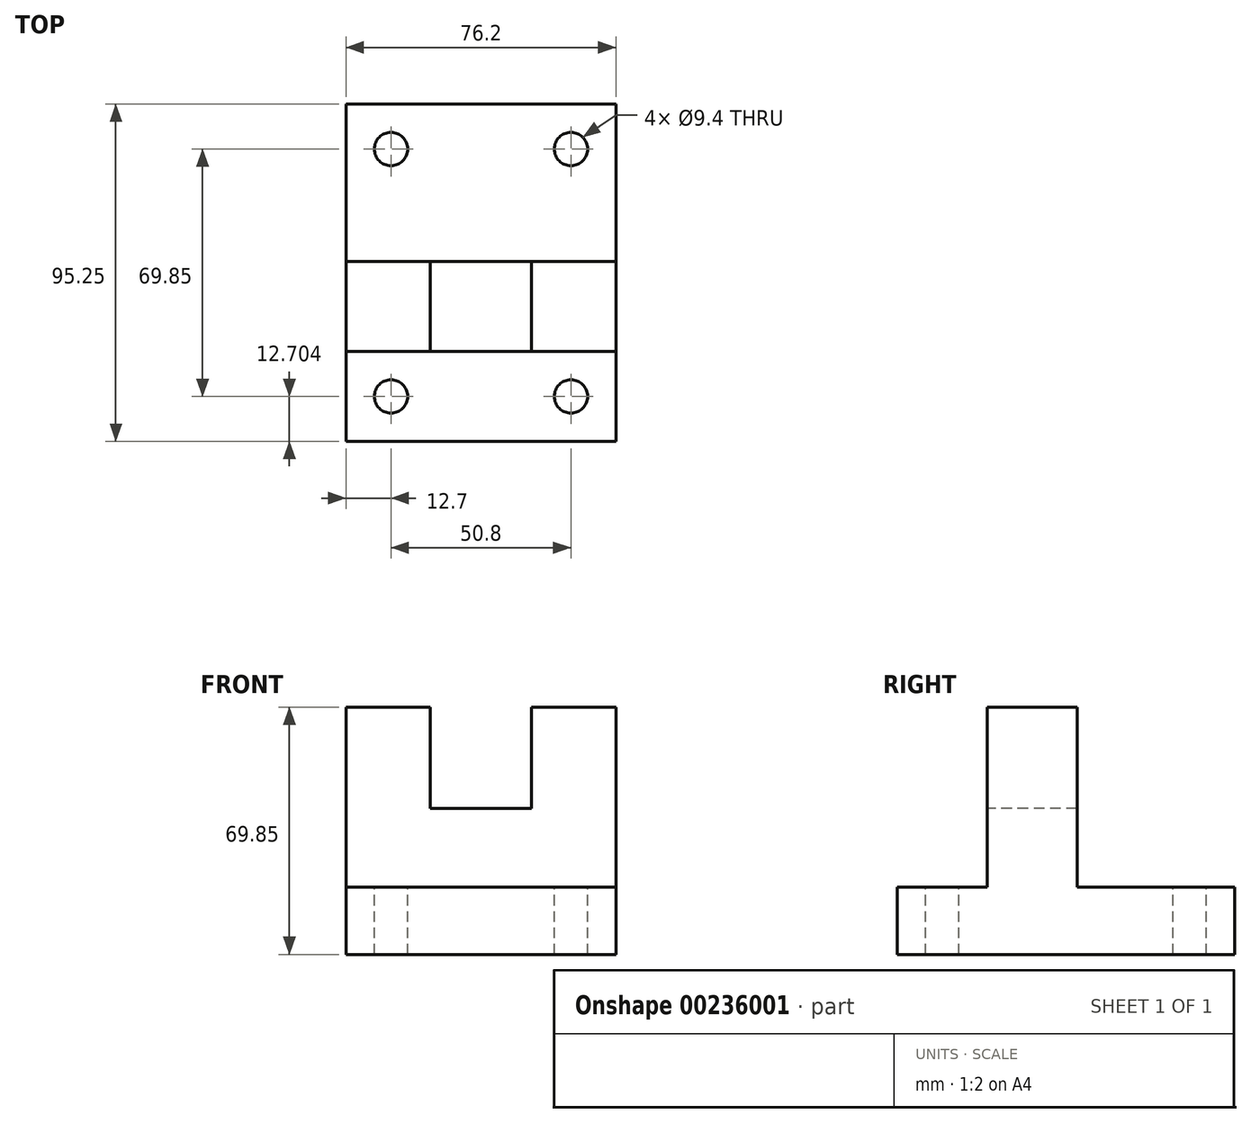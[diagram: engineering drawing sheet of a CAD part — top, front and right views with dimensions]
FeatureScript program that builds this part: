
annotation { "Feature Type Name" : "Feature", "Feature Type Description" : "" }
export const myFeature = defineFeature(function(context is Context, id is Id, definition is map)
    precondition{}
    {
        {
            var Q0;
            Q0=qCreatedBy(makeId("Right.planeOp"),FACE);
            var sketch = newSketch(context, id + "F0", { "sketchPlane" : qUnion([Q0])});
            skLineSegment(sketch, "E0", {"start": v(48.25, -12.1) * mm, "end": v(-47, -12.1) * mm});
            skLineSegment(sketch, "E1", {"start": v(-47, -12.1) * mm, "end": v(-47, 6.95) * mm});
            skLineSegment(sketch, "E2", {"start": v(-47, 6.95) * mm, "end": v(-21.6, 6.95) * mm});
            skLineSegment(sketch, "E3", {"start": v(-21.6, 6.95) * mm, "end": v(-21.6, 57.75) * mm});
            skLineSegment(sketch, "E4", {"start": v(-21.6, 57.75) * mm, "end": v(3.8, 57.75) * mm});
            skLineSegment(sketch, "E5", {"start": v(3.8, 57.75) * mm, "end": v(3.8, 6.95) * mm});
            skLineSegment(sketch, "E6", {"start": v(3.8, 6.95) * mm, "end": v(48.25, 6.95) * mm});
            skLineSegment(sketch, "E7", {"start": v(48.25, 6.95) * mm, "end": v(48.25, -12.1) * mm});
            skSolve(sketch);
        }
        {
            var Q0;
            Q0 = qSketchRegion(id + "F0", true);
            extrude(context, id + "F1", {"entities" : qUnion([Q0]), "depth" : 76.2 * mm});
        }
        {
            var Q0;
            Q0=makeQuery(id+"F1.opExtrude","SWEPT_FACE",FACE,{"disambiguationData":[OSD([sQuery(id+"F0.wireOp",EDGE,"E3")])]});
            var sketch = newSketch(context, id + "F2", { "sketchPlane" : qUnion([Q0])});
            skLineSegment(sketch, "E8", {"start": v(23.81, 57.75) * mm, "end": v(23.81, 29.17) * mm});
            skLineSegment(sketch, "E9", {"start": v(23.81, 29.17) * mm, "end": v(52.39, 29.17) * mm});
            skLineSegment(sketch, "E10", {"start": v(52.39, 29.17) * mm, "end": v(52.39, 57.75) * mm});
            skLineSegment(sketch, "E11", {"start": v(23.81, 57.75) * mm, "end": v(52.39, 57.75) * mm});
            skLineSegment(sketch, "E12", {"start": v(52.39, 57.75) * mm, "end": v(76.2, 57.75) * mm});
            skLineSegment(sketch, "E13", {"start": v(0, 57.75) * mm, "end": v(23.81, 57.75) * mm});
            skSolve(sketch);
        }
        {
            var Q0;
            Q0=makeQuery(id+"F2.imprint","IMPRINT",FACE,{"disambiguationData":[TD([[makeQuery(id+"F2.imprint","IMPRINT",EDGE,{"derivedFrom":sQuery(id+"F2.wireOp",EDGE,"E8")}),1.0]])]});
            extrude(context, id + "F3", {"entities" : qUnion([Q0]), "operationType" : NewBodyOperationType.REMOVE, "oppositeDirection" : true, "depth" : 25.4 * mm});
        }
        {
            var Q0;
            Q0=makeQuery(id+"F1.opExtrude","SWEPT_FACE",FACE,{"disambiguationData":[OSD([sQuery(id+"F0.wireOp",EDGE,"E6")])]});
            var sketch = newSketch(context, id + "F4", { "sketchPlane" : qUnion([Q0])});
            skCircle(sketch, "E14", {"center": v(63.5, 35.55) * mm, "radius": 4.7 * mm});
            skLineSegment(sketch, "E15", {"start": v(38.1, 48.25) * mm, "end": v(38.1, 67.12) * mm, "construction": true});
            skCircle(sketch, "E16.MirrorC", {"center": v(12.7, 35.55) * mm, "radius": 4.7 * mm});
            skSolve(sketch);
        }
        {
            var Q0;
            Q0 = qSketchRegion(id + "F4", true);
            extrude(context, id + "F5", {"entities" : qUnion([Q0]), "operationType" : NewBodyOperationType.REMOVE, "oppositeDirection" : true, "depth" : 25.4 * mm});
        }
        {
            var Q0;
            Q0=makeQuery(id+"F1.opExtrude","SWEPT_FACE",FACE,{"disambiguationData":[OSD([sQuery(id+"F0.wireOp",EDGE,"E2")])]});
            var sketch = newSketch(context, id + "F6", { "sketchPlane" : qUnion([Q0])});
            skCircle(sketch, "E17", {"center": v(63.5, -34.3) * mm, "radius": 4.7 * mm});
            skCircle(sketch, "E18", {"center": v(12.7, -34.3) * mm, "radius": 4.7 * mm});
            skSolve(sketch);
        }
        {
            var Q0;
            Q0 = qSketchRegion(id + "F6", true);
            extrude(context, id + "F7", {"entities" : qUnion([Q0]), "operationType" : NewBodyOperationType.REMOVE, "oppositeDirection" : true, "depth" : 25.4 * mm});
        }
    });
